# Revit family: Immergas-Ares pro 348
name_source: partatom
category: Attrezzatura meccanica
revit_build: Autodesk Revit 2018 (Build: 20181015_0930(x64)
units: mm (PartAtom-declared; Revit-internal decimal feet)

## family parameters
Basato su piano di lavoro = No
Condiviso = No
Punto di calcolo locali = No
Quota connettore circolare = Usa diametro
Sempre verticale = Sì
Taglio con vuoti quando caricato = No
Tipo di parte = Normale

## types (1)
- Immergas-Ares pro 348
    Case = Immergas - Alluminio
    Diameter of fume exhaust = 300 mm
    Dimensions of Piping Connectors = 38 mm
    ETIM Note = Residential heating
    Electric Power = 270 W
    Frequency of use = 50 Hz
    Hot water flow = 0.0 L/s
    Hydraulic Fittings = 2032 mm
    Manufacturer Product Link = https://www.immergas.com
    Mass = 716.00 kg
    MasterFormat = 23 00 00- Heating, Ventilating, and Air Conditioning (HVAC)
    Masterformat 2014 Description = Heating, Ventilating, and Air Conditioning (HVAC)
    Modello = Immergas-Ares pro 348
    Name BIM&CO = Caldaia
    Nominal Current = 6 A
    Nominal Voltage = 230 V
    Omniclass Description = HVAC Specific Products and Equipment
    Operating Temperature = 90 °C
    Overall Depth = 1273 mm  [stored 4.17651 ft]
    Overall Height = 2130 mm  [stored 6.98819 ft]
    Overall Width = 996 mm  [stored 3.26772 ft]
    Piping volume boiler = 0.34 m³
    Product Code = 3.028312
    Produttore = Immergas
    Thermal power 80/60°C = 341420 W
    UDP_334_495_PORTATA_TERMICA = 348
    UDP_88_494_GAS_CONNECTION_DIAMETER = 1.5
    Uniformat = Heat Generating Systems
    Uniformat II Description = Heat Generating Systems
    Uniformat code = D3020
    cerniere = Immergas - Plastica Nero
    yield hvac heating load nominal (%) = 98.11
    yield hvac heating load nominal 30 (%) = 97.41

note: [stored X ft] marks values corroborated as IEEE doubles in the binary element streams (Revit-internal decimal feet)
